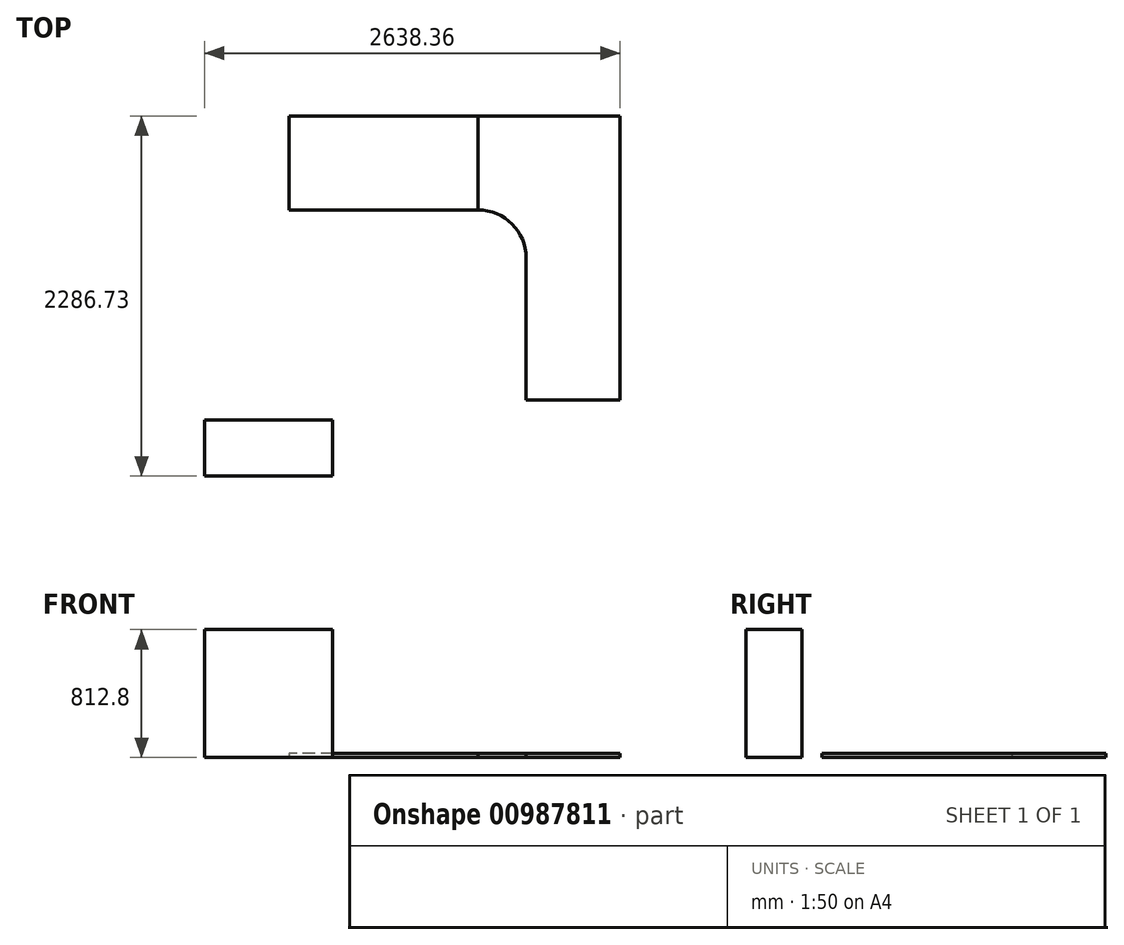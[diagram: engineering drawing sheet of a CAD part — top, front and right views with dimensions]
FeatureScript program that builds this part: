
annotation { "Feature Type Name" : "Feature", "Feature Type Description" : "" }
export const myFeature = defineFeature(function(context is Context, id is Id, definition is map)
    precondition{}
    {
        {
            var Q0;
            Q0=qCreatedBy(makeId("Top.planeOp"),FACE);
            var sketch = newSketch(context, id + "F0", { "sketchPlane" : qUnion([Q0])});
            skLineSegment(sketch, "E0.bottom", {"start": v(0, 0) * mm, "end": v(-1200.15, 0) * mm});
            skLineSegment(sketch, "E0.top", {"start": v(0, 596.9) * mm, "end": v(-1200.15, 596.9) * mm});
            skLineSegment(sketch, "E0.left", {"start": v(0, 0) * mm, "end": v(0, 596.9) * mm});
            skLineSegment(sketch, "E0.right", {"start": v(-1200.15, 0) * mm, "end": v(-1200.15, 596.9) * mm});
            skLineSegment(sketch, "E1.bottom", {"start": v(0, 596.9) * mm, "end": v(901.7, 596.9) * mm});
            skLineSegment(sketch, "E1.top", {"start": v(304.8, -1206.5) * mm, "end": v(901.7, -1206.5) * mm});
            skLineSegment(sketch, "E1.left", {"start": v(0, 596.9) * mm, "end": v(0, 0) * mm});
            skLineSegment(sketch, "E1.right", {"start": v(901.7, 596.9) * mm, "end": v(901.7, -1206.5) * mm});
            skLineSegment(sketch, "E2", {"start": v(304.8, -304.8) * mm, "end": v(304.8, -1206.5) * mm});
            skArc(sketch, "E3.filletArc", {"start": v(304.8, -304.8) * mm, "mid": v(215.53, -89.27) * mm, "end": v(0, 0) * mm});
            skLineSegment(sketch, "E4.bottom", {"start": v(-1736.66, -1689.83) * mm, "end": v(-923.86, -1689.83) * mm});
            skLineSegment(sketch, "E4.top", {"start": v(-1736.66, -1334.23) * mm, "end": v(-923.86, -1334.23) * mm});
            skLineSegment(sketch, "E4.left", {"start": v(-1736.66, -1689.83) * mm, "end": v(-1736.66, -1334.23) * mm});
            skLineSegment(sketch, "E4.right", {"start": v(-923.86, -1689.83) * mm, "end": v(-923.86, -1334.23) * mm});
            skSolve(sketch);
        }
        {
            var Q0;
            Q0=makeQuery(id+"F0.imprint","IMPRINT",FACE,{"disambiguationData":[TD([[makeQuery(id+"F0.imprint","IMPRINT",EDGE,{"derivedFrom":sQuery(id+"F0.wireOp",EDGE,"E0.bottom")}),-1.0]])]});
            extrude(context, id + "F1", {"entities" : qUnion([Q0]), "depth" : 25.4 * mm, "offsetDistance" : 25.4 * mm});
        }
        {
            var Q0;
            Q0=makeQuery(id+"F0.imprint","IMPRINT",FACE,{"disambiguationData":[TD([[makeQuery(id+"F0.imprint","IMPRINT",EDGE,{"derivedFrom":sQuery(id+"F0.wireOp",EDGE,"E1.bottom")}),-1.0]])]});
            extrude(context, id + "F2", {"entities" : qUnion([Q0]), "depth" : 25.4 * mm, "offsetDistance" : 25.4 * mm});
        }
        {
            var Q0;
            Q0=makeQuery(id+"F0.imprint","IMPRINT",FACE,{"disambiguationData":[TD([[makeQuery(id+"F0.imprint","IMPRINT",EDGE,{"derivedFrom":sQuery(id+"F0.wireOp",EDGE,"E4.bottom")}),1.0]])]});
            var sketch = newSketch(context, id + "F3", { "sketchPlane" : qUnion([Q0])});
            skSolve(sketch);
        }
        {
            var Q0;
            Q0=makeQuery(id+"F3.imprint","IMPRINT",FACE,{"disambiguationData":[TD([[makeQuery(id+"F3.imprint","IMPRINT",EDGE,{"derivedFrom":makeQuery(id+"F0.imprint","IMPRINT",EDGE,{"derivedFrom":sQuery(id+"F0.wireOp",EDGE,"E4.bottom")})}),1.0]])]});
            extrude(context, id + "F4", {"entities" : qUnion([Q0]), "depth" : 812.8 * mm, "offsetDistance" : 25.4 * mm});
        }
    });
